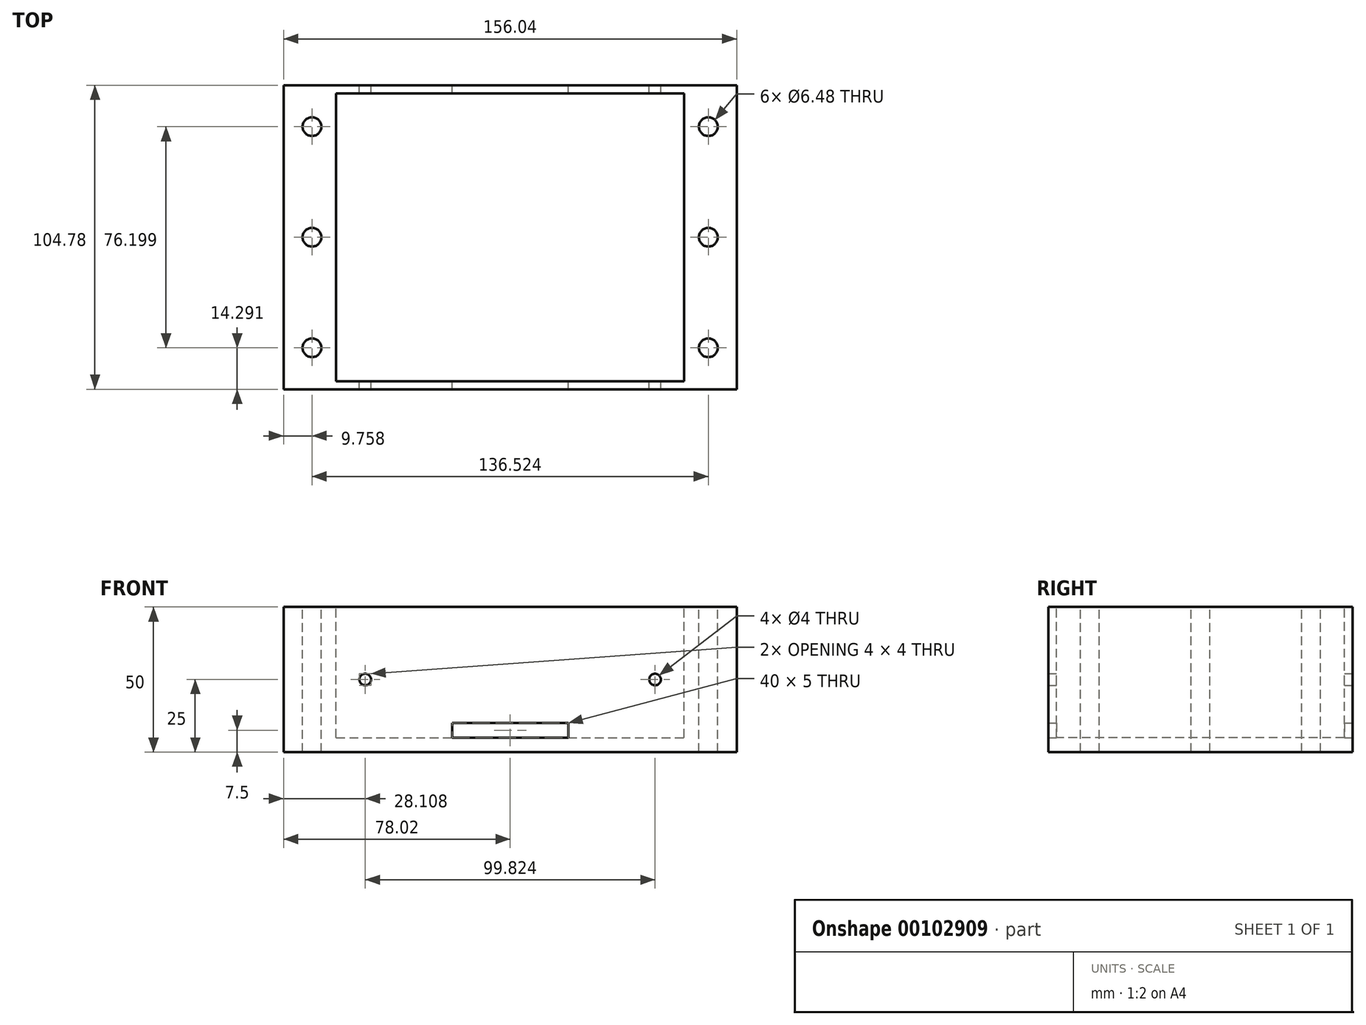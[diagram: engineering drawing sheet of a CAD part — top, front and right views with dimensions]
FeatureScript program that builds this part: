
annotation { "Feature Type Name" : "Feature", "Feature Type Description" : "" }
export const myFeature = defineFeature(function(context is Context, id is Id, definition is map)
    precondition{}
    {
        {
            var Q0;
            Q0=qCreatedBy(makeId("Top.planeOp"),FACE);
            var sketch = newSketch(context, id + "F0", { "sketchPlane" : qUnion([Q0])});
            skLineSegment(sketch, "E0", {"start": v(68.26, 31.75) * mm, "end": v(72.22, 31.75) * mm});
            skLineSegment(sketch, "E1", {"start": v(72.22, 6.35) * mm, "end": v(72.22, 31.75) * mm});
            skLineSegment(sketch, "E2", {"start": v(68.26, 6.35) * mm, "end": v(72.22, 6.35) * mm});
            skArc(sketch, "E3", {"start": v(68.26, 6.35) * mm, "mid": v(61.91, 0) * mm, "end": v(68.26, -6.35) * mm});
            skLineSegment(sketch, "E4", {"start": v(68.26, -6.35) * mm, "end": v(72.22, -6.35) * mm});
            skLineSegment(sketch, "E5", {"start": v(72.22, -31.75) * mm, "end": v(72.22, -6.35) * mm});
            skLineSegment(sketch, "E6", {"start": v(68.26, -31.75) * mm, "end": v(72.22, -31.75) * mm});
            skArc(sketch, "E7", {"start": v(68.26, -31.75) * mm, "mid": v(61.91, -38.1) * mm, "end": v(68.26, -44.45) * mm});
            skLineSegment(sketch, "E8", {"start": v(68.26, -44.45) * mm, "end": v(72.22, -44.45) * mm});
            skLineSegment(sketch, "E9", {"start": v(72.22, -51.59) * mm, "end": v(72.22, -44.45) * mm});
            skLineSegment(sketch, "E10", {"start": v(-72.23, -51.59) * mm, "end": v(72.23, -51.59) * mm});
            skLineSegment(sketch, "E11", {"start": v(-72.23, -51.59) * mm, "end": v(-72.23, -44.45) * mm});
            skLineSegment(sketch, "E12", {"start": v(-68.26, -44.45) * mm, "end": v(-72.23, -44.45) * mm});
            skArc(sketch, "E13", {"start": v(-68.26, -44.45) * mm, "mid": v(-61.91, -38.1) * mm, "end": v(-68.26, -31.75) * mm});
            skLineSegment(sketch, "E14", {"start": v(-68.26, -31.75) * mm, "end": v(-72.23, -31.75) * mm});
            skLineSegment(sketch, "E15", {"start": v(-72.23, -31.75) * mm, "end": v(-72.23, -6.35) * mm});
            skLineSegment(sketch, "E16", {"start": v(-68.26, -6.35) * mm, "end": v(-72.23, -6.35) * mm});
            skArc(sketch, "E17", {"start": v(-68.26, -6.35) * mm, "mid": v(-61.91, 0) * mm, "end": v(-68.26, 6.35) * mm});
            skLineSegment(sketch, "E18", {"start": v(-68.26, 6.35) * mm, "end": v(-72.23, 6.35) * mm});
            skLineSegment(sketch, "E19", {"start": v(-72.23, 6.35) * mm, "end": v(-72.23, 31.75) * mm});
            skLineSegment(sketch, "E20", {"start": v(-68.26, 31.75) * mm, "end": v(-72.23, 31.75) * mm});
            skArc(sketch, "E21", {"start": v(-68.26, 31.75) * mm, "mid": v(-61.91, 38.1) * mm, "end": v(-68.26, 44.45) * mm});
            skLineSegment(sketch, "E22", {"start": v(-68.26, 44.45) * mm, "end": v(-72.23, 44.45) * mm});
            skLineSegment(sketch, "E23", {"start": v(-72.23, 44.45) * mm, "end": v(-72.23, 51.59) * mm});
            skLineSegment(sketch, "E24", {"start": v(72.22, 51.59) * mm, "end": v(-72.23, 51.59) * mm});
            skLineSegment(sketch, "E25", {"start": v(72.22, 44.45) * mm, "end": v(72.22, 51.59) * mm});
            skLineSegment(sketch, "E26", {"start": v(68.26, 44.45) * mm, "end": v(72.22, 44.45) * mm});
            skArc(sketch, "E27", {"start": v(68.26, 44.45) * mm, "mid": v(61.91, 38.1) * mm, "end": v(68.26, 31.75) * mm});
            skCircle(sketch, "E28", {"center": v(-68.26, 0) * mm, "radius": 3.24 * mm});
            skCircle(sketch, "E29", {"center": v(-68.26, -38.1) * mm, "radius": 3.24 * mm});
            skCircle(sketch, "E30", {"center": v(68.26, 0) * mm, "radius": 3.24 * mm});
            skCircle(sketch, "E31", {"center": v(-68.26, 38.1) * mm, "radius": 3.24 * mm});
            skCircle(sketch, "E32", {"center": v(68.26, -38.1) * mm, "radius": 3.24 * mm});
            skCircle(sketch, "E33", {"center": v(68.26, 38.1) * mm, "radius": 3.24 * mm});
            skLineSegment(sketch, "E34", {"start": v(-73.03, -52.39) * mm, "end": v(-73.03, 52.39) * mm});
            skLineSegment(sketch, "E35", {"start": v(73.03, -52.39) * mm, "end": v(73.03, 52.39) * mm});
            skLineSegment(sketch, "E36", {"start": v(73.03, 52.39) * mm, "end": v(-73.03, 52.39) * mm});
            skLineSegment(sketch, "E37", {"start": v(-73.03, -52.39) * mm, "end": v(73.03, -52.39) * mm});
            skLineSegment(sketch, "E38.bottom", {"start": v(73.03, 52.39) * mm, "end": v(78.03, 52.39) * mm});
            skLineSegment(sketch, "E38.top", {"start": v(73.03, -52.39) * mm, "end": v(78.03, -52.39) * mm});
            skLineSegment(sketch, "E38.left", {"start": v(73.03, 52.39) * mm, "end": v(73.03, -52.39) * mm});
            skLineSegment(sketch, "E38.right", {"start": v(78.03, 52.39) * mm, "end": v(78.03, -52.39) * mm});
            skLineSegment(sketch, "E39.MirrorCS", {"start": v(-73.03, -52.39) * mm, "end": v(-78.03, -52.39) * mm});
            skLineSegment(sketch, "E40.MirrorCS", {"start": v(-78.03, 52.39) * mm, "end": v(-78.03, -52.39) * mm});
            skLineSegment(sketch, "E41.MirrorCS", {"start": v(-73.03, 52.39) * mm, "end": v(-78.03, 52.39) * mm});
            skSolve(sketch);
        }
        {
            var Q0;
            Q0=qSketchRegion(id+"F0",true);
            var Q1;
            Q1=makeQuery(id+"F0.imprint","IMPRINT",FACE,{"disambiguationData":[TD([[makeQuery(id+"F0.imprint","IMPRINT",EDGE,{"derivedFrom":sQuery(id+"F0.wireOp",EDGE,"E31")}),-1.0]])]});
            var Q2;
            Q2=makeQuery(id+"F0.imprint","IMPRINT",FACE,{"disambiguationData":[TD([[makeQuery(id+"F0.imprint","IMPRINT",EDGE,{"derivedFrom":sQuery(id+"F0.wireOp",EDGE,"E6")}),1.0]])]});
            var Q3;
            Q3=makeQuery(id+"F0.imprint","IMPRINT",FACE,{"disambiguationData":[TD([[makeQuery(id+"F0.imprint","IMPRINT",EDGE,{"derivedFrom":sQuery(id+"F0.wireOp",EDGE,"E28")}),-1.0]])]});
            var Q4;
            Q4=makeQuery(id+"F0.imprint","IMPRINT",FACE,{"disambiguationData":[TD([[makeQuery(id+"F0.imprint","IMPRINT",EDGE,{"derivedFrom":sQuery(id+"F0.wireOp",EDGE,"E29")}),-1.0]])]});
            var Q5;
            Q5=makeQuery(id+"F0.imprint","IMPRINT",FACE,{"disambiguationData":[TD([[makeQuery(id+"F0.imprint","IMPRINT",EDGE,{"derivedFrom":sQuery(id+"F0.wireOp",EDGE,"E32")}),-1.0]])]});
            var Q6;
            Q6=makeQuery(id+"F0.imprint","IMPRINT",FACE,{"disambiguationData":[TD([[makeQuery(id+"F0.imprint","IMPRINT",EDGE,{"derivedFrom":sQuery(id+"F0.wireOp",EDGE,"E30")}),-1.0]])]});
            var Q7;
            Q7=makeQuery(id+"F0.imprint","IMPRINT",FACE,{"disambiguationData":[TD([[makeQuery(id+"F0.imprint","IMPRINT",EDGE,{"derivedFrom":sQuery(id+"F0.wireOp",EDGE,"E33")}),-1.0]])]});
            extrude(context, id + "F1", {"entities" : qUnion([Q0, Q1, Q2, Q3, Q4, Q5, Q6, Q7]), "oppositeDirection" : true, "depth" : 50 * mm});
        }
        {
            var Q0;
            Q0=makeQuery(id+"F0.imprint","IMPRINT",FACE,{"disambiguationData":[TD([[makeQuery(id+"F0.imprint","IMPRINT",EDGE,{"derivedFrom":sQuery(id+"F0.wireOp",EDGE,"E6")}),1.0]])]});
            var sketch = newSketch(context, id + "F2", { "sketchPlane" : qUnion([Q0])});
            skLineSegment(sketch, "E42.bottom", {"start": v(-59.91, 49.59) * mm, "end": v(59.91, 49.59) * mm});
            skLineSegment(sketch, "E42.top", {"start": v(-59.91, -49.59) * mm, "end": v(59.91, -49.59) * mm});
            skLineSegment(sketch, "E42.left", {"start": v(-59.91, 49.59) * mm, "end": v(-59.91, -49.59) * mm});
            skLineSegment(sketch, "E42.right", {"start": v(59.91, 49.59) * mm, "end": v(59.91, -49.59) * mm});
            skPoint(sketch, "E42.middle", {"position": v(0, 0) * mm});
            skSolve(sketch);
        }
        {
            var Q0;
            Q0=qSketchRegion(id+"F2",true);
            extrude(context, id + "F3", {"entities" : qUnion([Q0]), "operationType" : NewBodyOperationType.REMOVE, "oppositeDirection" : true, "depth" : 45 * mm});
        }
        {
            var Q0;
            Q0=sQuery(id+"F0.wireOp",VERTEX,"E21.center");
            var Q1;
            Q1=sQuery(id+"F0.wireOp",VERTEX,"E17.center");
            var Q2;
            Q2=sQuery(id+"F0.wireOp",VERTEX,"E13.center");
            var Q3;
            Q3=sQuery(id+"F0.wireOp",VERTEX,"E7.center");
            var Q4;
            Q4=sQuery(id+"F0.wireOp",VERTEX,"E27.center");
            var Q5;
            Q5=sQuery(id+"F0.wireOp",VERTEX,"E3.center");
            var Q6;
            Q6=makeQuery(id+"F1.opExtrude","SWEPT_BODY",BODY,{"disambiguationData":[OSD([sQuery(id+"F0.wireOp",EDGE,"E36"),sQuery(id+"F0.wireOp",EDGE,"E37"),sQuery(id+"F0.wireOp",EDGE,"E38.bottom"),sQuery(id+"F0.wireOp",EDGE,"E38.top"),sQuery(id+"F0.wireOp",EDGE,"E38.right"),sQuery(id+"F0.wireOp",EDGE,"E39.MirrorCS"),sQuery(id+"F0.wireOp",EDGE,"E40.MirrorCS"),sQuery(id+"F0.wireOp",EDGE,"E41.MirrorCS")])]});
            hole(context, id + "F4", {"style" : HoleStyle.SIMPLE, "endStyle" : HoleEndStyle.BLIND, "holeDiameter" : 5.6 * mm, "holeDepth" : 20 * mm, "locations" : qUnion([Q0, Q1, Q2, Q3, Q4, Q5]), "scope" : qUnion([Q6])});
        }
        {
            var Q0;
            Q0=makeQuery(id+"F1.opExtrude","SWEPT_FACE",FACE,{"disambiguationData":[OSD([sQuery(id+"F0.wireOp",EDGE,"E36"),sQuery(id+"F0.wireOp",EDGE,"E38.bottom"),sQuery(id+"F0.wireOp",EDGE,"E41.MirrorCS")])]});
            var sketch = newSketch(context, id + "F5", { "sketchPlane" : qUnion([Q0])});
            skLineSegment(sketch, "E43.bottom", {"start": v(20, -45) * mm, "end": v(-20, -45) * mm});
            skLineSegment(sketch, "E43.top", {"start": v(20, -40) * mm, "end": v(-20, -40) * mm});
            skLineSegment(sketch, "E43.left", {"start": v(20, -45) * mm, "end": v(20, -40) * mm});
            skLineSegment(sketch, "E43.right", {"start": v(-20, -45) * mm, "end": v(-20, -40) * mm});
            skPoint(sketch, "E43.middle", {"position": v(0, -42.5) * mm});
            skPoint(sketch, "E44", {"position": v(-49.91, -25) * mm});
            skPoint(sketch, "E44.positionSnap0", {"position": v(-78.03, -25) * mm});
            skPoint(sketch, "E45.MirrorP", {"position": v(49.91, -25) * mm});
            skSolve(sketch);
        }
        {
            var Q0;
            Q0=makeQuery(id+"F5.imprint","IMPRINT",FACE,{"disambiguationData":[TD([[makeQuery(id+"F5.imprint","IMPRINT",EDGE,{"derivedFrom":sQuery(id+"F5.wireOp",EDGE,"E43.bottom")}),-1.0]])]});
            extrude(context, id + "F6", {"entities" : qUnion([Q0]), "operationType" : NewBodyOperationType.REMOVE, "endBound" : BoundingType.THROUGH_ALL, "oppositeDirection" : true, "depth" : 25 * mm});
        }
        {
            var Q0;
            Q0=sQuery(id+"F5.wireOp",VERTEX,"E44");
            var Q1;
            Q1=sQuery(id+"F5.wireOp",VERTEX,"E45.MirrorP");
            var Q2;
            Q2=makeQuery(id+"F1.opExtrude","SWEPT_BODY",BODY,{"disambiguationData":[OSD([sQuery(id+"F0.wireOp",EDGE,"E36"),sQuery(id+"F0.wireOp",EDGE,"E37"),sQuery(id+"F0.wireOp",EDGE,"E38.bottom"),sQuery(id+"F0.wireOp",EDGE,"E38.top"),sQuery(id+"F0.wireOp",EDGE,"E38.right"),sQuery(id+"F0.wireOp",EDGE,"E39.MirrorCS"),sQuery(id+"F0.wireOp",EDGE,"E40.MirrorCS"),sQuery(id+"F0.wireOp",EDGE,"E41.MirrorCS")])]});
            hole(context, id + "F7", {"style" : HoleStyle.SIMPLE, "endStyle" : HoleEndStyle.THROUGH, "holeDiameter" : 4 * mm, "locations" : qUnion([Q0, Q1]), "scope" : qUnion([Q2]), "isTappedThrough" : true});
        }
    });
